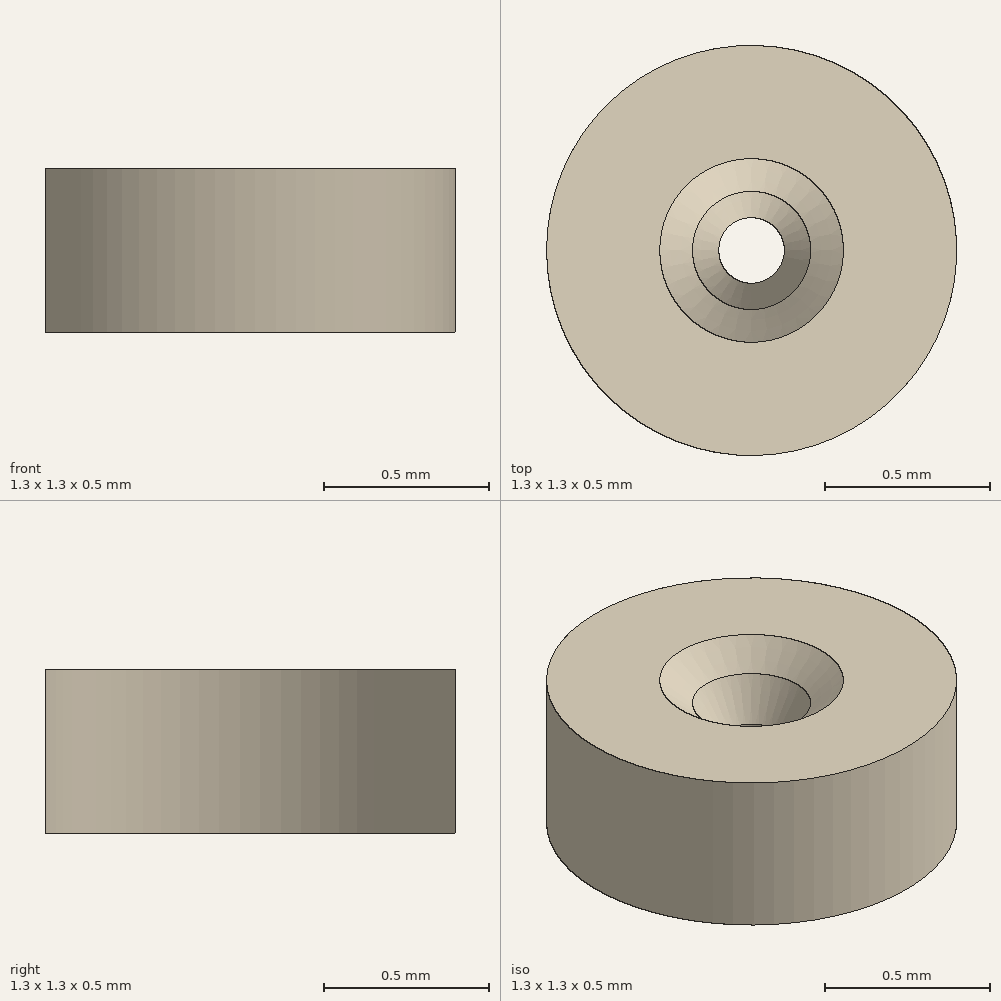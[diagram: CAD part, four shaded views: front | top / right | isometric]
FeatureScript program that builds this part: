
annotation { "Feature Type Name" : "Feature", "Feature Type Description" : "" }
export const myFeature = defineFeature(function(context is Context, id is Id, definition is map)
    precondition{}
    {
        {
            var Q0;
            Q0=qCreatedBy(makeId("Right.planeOp"),FACE);
            var sketch = newSketch(context, id + "F0", { "sketchPlane" : qUnion([Q0])});
            skLineSegment(sketch, "E0", {"start": v(-0.1, 0) * mm, "end": v(-0.63, 0) * mm});
            skLineSegment(sketch, "E1", {"start": v(-0.63, 0) * mm, "end": v(-0.63, 0.5) * mm});
            skLineSegment(sketch, "E2", {"start": v(-0.63, 0.5) * mm, "end": v(-0.28, 0.5) * mm});
            skLineSegment(sketch, "E3", {"start": v(-0.28, 0.5) * mm, "end": v(-0.28, 0.42) * mm});
            skLineSegment(sketch, "E4", {"start": v(-0.28, 0.42) * mm, "end": v(-0.18, 0.42) * mm});
            skLineSegment(sketch, "E5", {"start": v(-0.18, 0.42) * mm, "end": v(-0.18, 0.29) * mm});
            skLineSegment(sketch, "E6", {"start": v(-0.18, 0.29) * mm, "end": v(-0.1, 0.29) * mm});
            skLineSegment(sketch, "E7", {"start": v(-0.1, 0.29) * mm, "end": v(-0.18, 0.42) * mm});
            skLineSegment(sketch, "E8", {"start": v(-0.28, 0.5) * mm, "end": v(-0.18, 0.42) * mm});
            skLineSegment(sketch, "E9", {"start": v(-0.1, 0.29) * mm, "end": v(-0.1, 0) * mm});
            skPoint(sketch, "E10.orphan", {"position": v(0, 0) * mm});
            skLineSegment(sketch, "E11", {"start": v(0, 0) * mm, "end": v(0, 0.07) * mm});
            skSolve(sketch);
        }
        {
            var Q0;
            Q0=makeQuery(id+"F0.imprint","IMPRINT",FACE,{"disambiguationData":[TD([[makeQuery(id+"F0.imprint","IMPRINT",EDGE,{"derivedFrom":sQuery(id+"F0.wireOp",EDGE,"E0")}),-1.0]])]});
            var Q1;
            Q1=makeQuery(id+"F0.imprint","IMPRINT",FACE,{"disambiguationData":[TD([[makeQuery(id+"F0.imprint","IMPRINT",EDGE,{"derivedFrom":sQuery(id+"F0.wireOp",EDGE,"E3")}),1.0]])]});
            var Q2;
            Q2=makeQuery(id+"F0.imprint","IMPRINT",FACE,{"disambiguationData":[TD([[makeQuery(id+"F0.imprint","IMPRINT",EDGE,{"derivedFrom":sQuery(id+"F0.wireOp",EDGE,"E5")}),1.0]])]});
            var Q3;
            Q3=sQuery(id+"F0.wireOp",EDGE,"E11");
            revolve(context, id + "F1", {"entities" : qUnion([Q0, Q1, Q2]), "axis" : qUnion([Q3]), "revolveType" : RevolveType.FULL});
        }
    });
